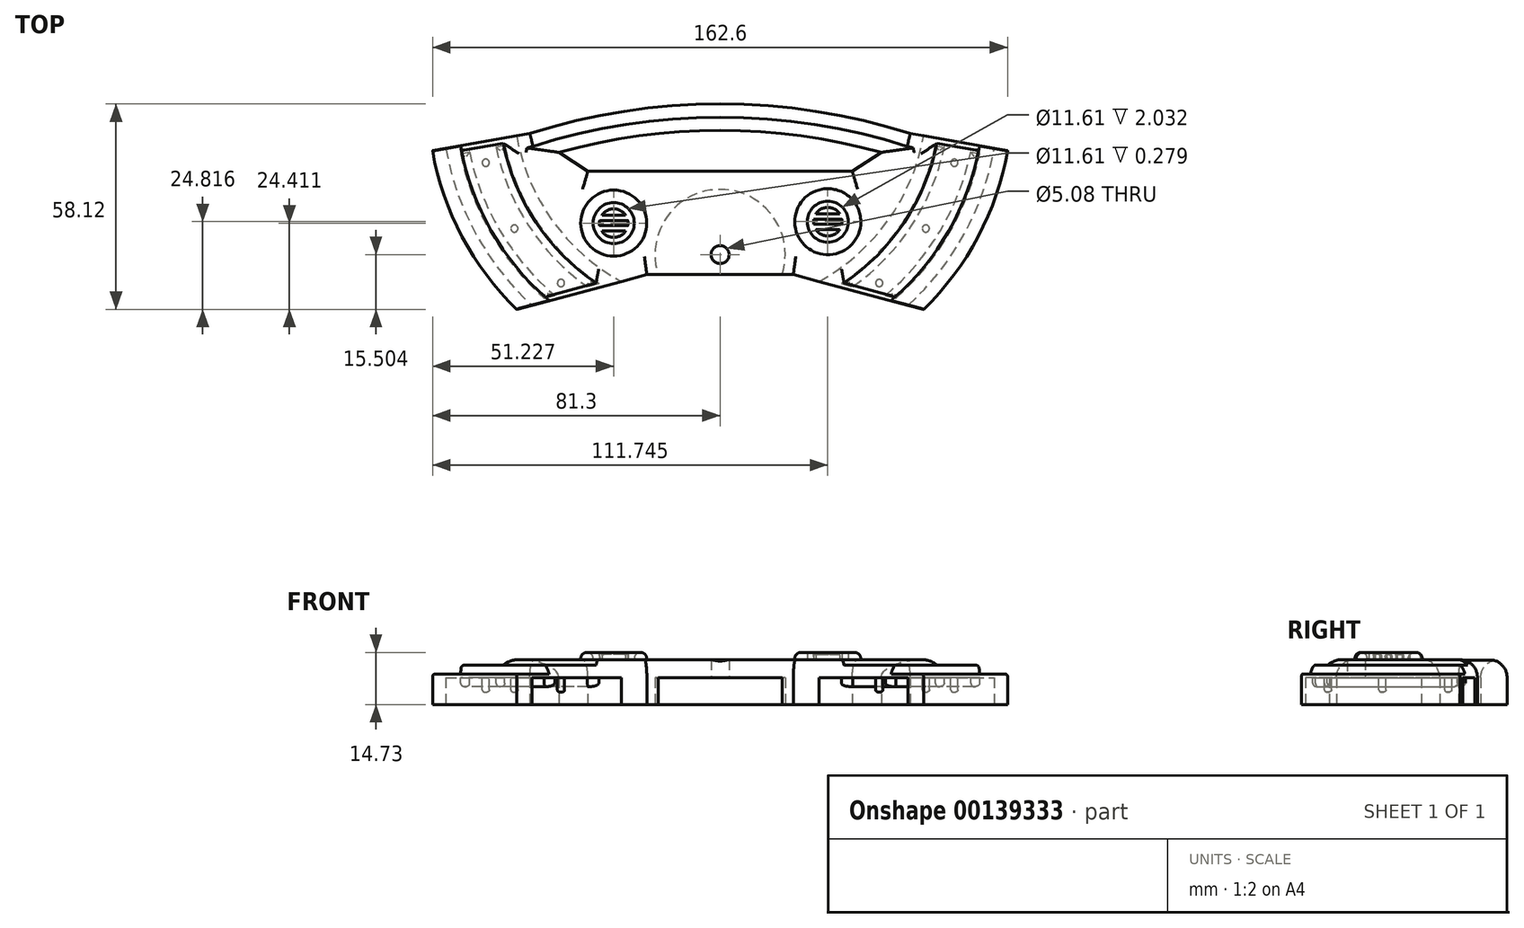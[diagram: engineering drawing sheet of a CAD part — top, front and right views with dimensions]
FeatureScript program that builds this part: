
annotation { "Feature Type Name" : "Feature", "Feature Type Description" : "" }
export const myFeature = defineFeature(function(context is Context, id is Id, definition is map)
    precondition{}
    {
        {
            var Q0;
            Q0=qCreatedBy(makeId("Top.planeOp"),FACE);
            var sketch = newSketch(context, id + "F0", { "sketchPlane" : qUnion([Q0])});
            skCircle(sketch, "E0", {"center": v(0, 0) * mm, "radius": 76.2 * mm, "construction": true});
            skCircle(sketch, "E1", {"center": v(0, 0) * mm, "radius": 60.96 * mm, "construction": true});
            skArc(sketch, "E2", {"start": v(-81.3, -14.33) * mm, "mid": v(-72.94, -38.65) * mm, "end": v(-57.5, -59.22) * mm});
            skLineSegment(sketch, "E3", {"start": v(0, 0) * mm, "end": v(-81.3, -14.33) * mm, "construction": true});
            skArc(sketch, "E4", {"start": v(81.3, -14.33) * mm, "mid": v(72.94, -38.65) * mm, "end": v(57.5, -59.22) * mm});
            skLineSegment(sketch, "E5", {"start": v(81.3, -14.33) * mm, "end": v(0, 0) * mm, "construction": true});
            skLineSegment(sketch, "E6", {"start": v(81.3, -14.33) * mm, "end": v(57.5, -59.22) * mm, "construction": true});
            skLineSegment(sketch, "E7", {"start": v(-81.3, -14.33) * mm, "end": v(-57.5, -59.22) * mm, "construction": true});
            skLineSegment(sketch, "E8", {"start": v(57.5, -59.22) * mm, "end": v(20.7, -49.36) * mm});
            skLineSegment(sketch, "E9", {"start": v(20.7, -49.36) * mm, "end": v(-20.7, -49.36) * mm});
            skLineSegment(sketch, "E10", {"start": v(-20.7, -49.36) * mm, "end": v(-57.5, -59.22) * mm});
            skLineSegment(sketch, "E11", {"start": v(-81.3, -14.33) * mm, "end": v(-53.78, -9.48) * mm});
            skLineSegment(sketch, "E12", {"start": v(-45.58, -14.8) * mm, "end": v(-37.38, -20.13) * mm});
            skLineSegment(sketch, "E13", {"start": v(-37.38, -20.13) * mm, "end": v(37.38, -20.13) * mm});
            skLineSegment(sketch, "E14", {"start": v(37.38, -20.13) * mm, "end": v(45.58, -14.8) * mm});
            skLineSegment(sketch, "E15", {"start": v(53.78, -9.48) * mm, "end": v(81.3, -14.33) * mm});
            skLineSegment(sketch, "E16", {"start": v(0, 0) * mm, "end": v(0, -177.8) * mm, "construction": true});
            skArc(sketch, "E17", {"start": v(-53.78, -9.48) * mm, "mid": v(0, -1.1) * mm, "end": v(53.78, -9.48) * mm});
            skArc(sketch, "E18", {"start": v(45.58, -14.8) * mm, "mid": v(0, -8.56) * mm, "end": v(-45.58, -14.8) * mm});
            skSolve(sketch);
        }
        {
            var Q0;
            Q0 = qSketchRegion(id + "F0", true);
            extrude(context, id + "F1", {"entities" : qUnion([Q0]), "depth" : 12.7 * mm});
        }
        {
            var Q0;
            Q0=qCreatedBy(makeId("Front.planeOp"),FACE);
            var sketch = newSketch(context, id + "F2", { "sketchPlane" : qUnion([Q0])});
            skLineSegment(sketch, "E19", {"start": v(62.5, 16.37) * mm, "end": v(62.5, 11.1) * mm});
            skLineSegment(sketch, "E20", {"start": v(62.5, 11.1) * mm, "end": v(74.5, 11.1) * mm});
            skLineSegment(sketch, "E21", {"start": v(74.5, 11.1) * mm, "end": v(74.5, 8.65) * mm});
            skLineSegment(sketch, "E22", {"start": v(74.5, 8.65) * mm, "end": v(83.99, 8.65) * mm});
            skLineSegment(sketch, "E23", {"start": v(83.99, 8.65) * mm, "end": v(83.99, 15.75) * mm});
            skLineSegment(sketch, "E24", {"start": v(83.99, 15.75) * mm, "end": v(62.5, 16.37) * mm});
            skSolve(sketch);
        }
        {
            var Q0;
            Q0=qCreatedBy(makeId("Front.planeOp"),FACE);
            var sketch = newSketch(context, id + "F3", { "sketchPlane" : qUnion([Q0])});
            skLineSegment(sketch, "E25", {"start": v(0, 99.5) * mm, "end": v(0, -112.08) * mm, "construction": true});
            skSolve(sketch);
        }
        {
            var Q0;
            Q0 = qSketchRegion(id + "F2", true);
            var Q1;
            Q1=sQuery(id+"F3.wireOp",EDGE,"E25");
            revolve(context, id + "F4", {"operationType" : NewBodyOperationType.REMOVE, "entities" : qUnion([Q0]), "axis" : qUnion([Q1]), "revolveType" : RevolveType.FULL, "oppositeDirection" : true});
        }
        {
            var Q0;
            Q0=makeQuery(id+"F1.opExtrude","CAP_FACE",FACE,{"disambiguationData":[OSD([sQuery(id+"F0.wireOp",EDGE,"E2"),sQuery(id+"F0.wireOp",EDGE,"E4"),sQuery(id+"F0.wireOp",EDGE,"E8"),sQuery(id+"F0.wireOp",EDGE,"E9"),sQuery(id+"F0.wireOp",EDGE,"E10"),sQuery(id+"F0.wireOp",EDGE,"E11"),sQuery(id+"F0.wireOp",EDGE,"E12"),sQuery(id+"F0.wireOp",EDGE,"E13"),sQuery(id+"F0.wireOp",EDGE,"E14"),sQuery(id+"F0.wireOp",EDGE,"E15"),sQuery(id+"F0.wireOp",EDGE,"E17"),sQuery(id+"F0.wireOp",EDGE,"E18")])],"isStart":false});
            fillet(context, id + "F5", {"entities" : qUnion([Q0]), "radius" : 5.08 * mm, "tangentPropagation" : true, "allowEdgeOverflow" : false});
        }
        {
            var Q0;
            Q0=makeQuery(id+"F1.opExtrude","CAP_FACE",FACE,{"disambiguationData":[OSD([sQuery(id+"F0.wireOp",EDGE,"E2"),sQuery(id+"F0.wireOp",EDGE,"E4"),sQuery(id+"F0.wireOp",EDGE,"E8"),sQuery(id+"F0.wireOp",EDGE,"E9"),sQuery(id+"F0.wireOp",EDGE,"E10"),sQuery(id+"F0.wireOp",EDGE,"E11"),sQuery(id+"F0.wireOp",EDGE,"E12"),sQuery(id+"F0.wireOp",EDGE,"E13"),sQuery(id+"F0.wireOp",EDGE,"E14"),sQuery(id+"F0.wireOp",EDGE,"E15"),sQuery(id+"F0.wireOp",EDGE,"E17"),sQuery(id+"F0.wireOp",EDGE,"E18")])],"isStart":false});
            var sketch = newSketch(context, id + "F6", { "sketchPlane" : qUnion([Q0])});
            skLineSegment(sketch, "E26", {"start": v(38.88, -25.21) * mm, "end": v(34.33, -47.75) * mm, "construction": true});
            skLineSegment(sketch, "E27", {"start": v(34.33, -47.75) * mm, "end": v(56.82, -15.18) * mm, "construction": true});
            skLineSegment(sketch, "E28", {"start": v(56.82, -15.18) * mm, "end": v(-56.82, -15.18) * mm, "construction": true});
            skLineSegment(sketch, "E29", {"start": v(-56.82, -15.18) * mm, "end": v(-34.33, -47.75) * mm, "construction": true});
            skLineSegment(sketch, "E30", {"start": v(-34.33, -47.75) * mm, "end": v(-38.88, -25.21) * mm, "construction": true});
            skLineSegment(sketch, "E31", {"start": v(-38.88, -25.21) * mm, "end": v(46.13, -36.48) * mm, "construction": true});
            skPoint(sketch, "E31.endSnap0", {"position": v(-36.6, -36.48) * mm});
            skLineSegment(sketch, "E32", {"start": v(46.13, -36.48) * mm, "end": v(-42.1, -36.48) * mm, "construction": true});
            skLineSegment(sketch, "E33", {"start": v(-42.1, -36.48) * mm, "end": v(38.88, -25.21) * mm, "construction": true});
            skLineSegment(sketch, "E34", {"start": v(21.38, -44.28) * mm, "end": v(38.88, -25.21) * mm, "construction": true});
            skLineSegment(sketch, "E35", {"start": v(-21.38, -44.28) * mm, "end": v(-38.88, -25.21) * mm, "construction": true});
            skCircle(sketch, "E36", {"center": v(30.44, -34.4) * mm, "radius": 9.33 * mm});
            skCircle(sketch, "E37", {"center": v(-30.07, -34.8) * mm, "radius": 9.33 * mm});
            skCircle(sketch, "E38", {"center": v(-30.07, -34.8) * mm, "radius": 5.8 * mm});
            skCircle(sketch, "E39", {"center": v(30.44, -34.4) * mm, "radius": 5.8 * mm});
            skSolve(sketch);
        }
        {
            var Q0;
            Q0 = qSketchRegion(id + "F6", true);
            extrude(context, id + "F7", {"entities" : qUnion([Q0]), "operationType" : NewBodyOperationType.ADD, "depth" : 2.03 * mm});
        }
        {
            var Q0;
            Q0=makeQuery(id+"F7.opExtrude","CAP_FACE",FACE,{"disambiguationData":[OSD([sQuery(id+"F6.wireOp",EDGE,"E37"),sQuery(id+"F6.wireOp",EDGE,"E38")])],"isStart":false});
            var Q1;
            Q1=makeQuery(id+"F7.opExtrude","CAP_EDGE",EDGE,{"disambiguationData":[OSD([sQuery(id+"F6.wireOp",EDGE,"E36")])],"isStart":false});
            fillet(context, id + "F8", {"entities" : qUnion([Q0, Q1]), "radius" : 1.75 * mm, "tangentPropagation" : true, "allowEdgeOverflow" : false});
        }
        {
            var Q0;
            Q0=makeQuery(id+"F7.boolean.opBoolean","SPLIT",FACE,{"disambiguationData":[TD([makeQuery(id+"F7.opExtrude","SWEPT_FACE",FACE,{"disambiguationData":[OSD([sQuery(id+"F6.wireOp",EDGE,"E38")])]})])],"derivedFrom":makeQuery(id+"F1.opExtrude","CAP_FACE",FACE,{"disambiguationData":[OSD([sQuery(id+"F0.wireOp",EDGE,"E2"),sQuery(id+"F0.wireOp",EDGE,"E4"),sQuery(id+"F0.wireOp",EDGE,"E8"),sQuery(id+"F0.wireOp",EDGE,"E9"),sQuery(id+"F0.wireOp",EDGE,"E10"),sQuery(id+"F0.wireOp",EDGE,"E11"),sQuery(id+"F0.wireOp",EDGE,"E12"),sQuery(id+"F0.wireOp",EDGE,"E13"),sQuery(id+"F0.wireOp",EDGE,"E14"),sQuery(id+"F0.wireOp",EDGE,"E15"),sQuery(id+"F0.wireOp",EDGE,"E17"),sQuery(id+"F0.wireOp",EDGE,"E18")])],"isStart":false})});
            var sketch = newSketch(context, id + "F9", { "sketchPlane" : qUnion([Q0])});
            skArc(sketch, "E40", {"start": v(-34.04, -34.07) * mm, "mid": v(-34.11, -34.8) * mm, "end": v(-34.04, -35.55) * mm});
            skLineSegment(sketch, "E41", {"start": v(-26.73, -32.55) * mm, "end": v(-33.42, -32.55) * mm});
            skLineSegment(sketch, "E42", {"start": v(-26.1, -34.07) * mm, "end": v(-34.04, -34.07) * mm});
            skLineSegment(sketch, "E43", {"start": v(-26.1, -35.55) * mm, "end": v(-34.04, -35.55) * mm});
            skLineSegment(sketch, "E44", {"start": v(-33.42, -37.07) * mm, "end": v(-26.73, -37.07) * mm});
            skArc(sketch, "E45.trimOffspring", {"start": v(-26.73, -32.55) * mm, "mid": v(-30.07, -30.77) * mm, "end": v(-33.42, -32.55) * mm});
            skArc(sketch, "E46.trimOffspring", {"start": v(-26.1, -35.55) * mm, "mid": v(-26.03, -34.8) * mm, "end": v(-26.1, -34.07) * mm});
            skArc(sketch, "E47.trimOffspring", {"start": v(-33.42, -37.07) * mm, "mid": v(-30.07, -38.85) * mm, "end": v(-26.73, -37.07) * mm});
            skSolve(sketch);
        }
        {
            var Q0;
            Q0=makeQuery(id+"F7.boolean.opBoolean","SPLIT",FACE,{"disambiguationData":[TD([makeQuery(id+"F7.opExtrude","SWEPT_FACE",FACE,{"disambiguationData":[OSD([sQuery(id+"F6.wireOp",EDGE,"E39")])]})])],"derivedFrom":makeQuery(id+"F1.opExtrude","CAP_FACE",FACE,{"disambiguationData":[OSD([sQuery(id+"F0.wireOp",EDGE,"E2"),sQuery(id+"F0.wireOp",EDGE,"E4"),sQuery(id+"F0.wireOp",EDGE,"E8"),sQuery(id+"F0.wireOp",EDGE,"E9"),sQuery(id+"F0.wireOp",EDGE,"E10"),sQuery(id+"F0.wireOp",EDGE,"E11"),sQuery(id+"F0.wireOp",EDGE,"E12"),sQuery(id+"F0.wireOp",EDGE,"E13"),sQuery(id+"F0.wireOp",EDGE,"E14"),sQuery(id+"F0.wireOp",EDGE,"E15"),sQuery(id+"F0.wireOp",EDGE,"E17"),sQuery(id+"F0.wireOp",EDGE,"E18")])],"isStart":false})});
            var sketch = newSketch(context, id + "F10", { "sketchPlane" : qUnion([Q0])});
            skArc(sketch, "E48", {"start": v(33.8, -32.14) * mm, "mid": v(30.44, -30.37) * mm, "end": v(27.1, -32.14) * mm});
            skLineSegment(sketch, "E49", {"start": v(27.1, -32.14) * mm, "end": v(33.8, -32.14) * mm});
            skLineSegment(sketch, "E50", {"start": v(34.42, -33.67) * mm, "end": v(26.47, -33.67) * mm});
            skLineSegment(sketch, "E51", {"start": v(26.47, -35.14) * mm, "end": v(34.42, -35.14) * mm});
            skLineSegment(sketch, "E52", {"start": v(33.8, -36.67) * mm, "end": v(27.1, -36.67) * mm});
            skArc(sketch, "E53.trimOffspring", {"start": v(26.47, -33.67) * mm, "mid": v(26.4, -34.4) * mm, "end": v(26.47, -35.14) * mm});
            skArc(sketch, "E54.trimOffspring", {"start": v(27.1, -36.67) * mm, "mid": v(30.44, -38.44) * mm, "end": v(33.8, -36.67) * mm});
            skArc(sketch, "E55.trimOffspring", {"start": v(34.42, -35.14) * mm, "mid": v(34.48, -34.4) * mm, "end": v(34.42, -33.67) * mm});
            skSolve(sketch);
        }
        {
            var Q0;
            Q0 = qSketchRegion(id + "F9", true);
            extrude(context, id + "F11", {"entities" : qUnion([Q0]), "operationType" : NewBodyOperationType.ADD, "depth" : 1.52 * mm});
        }
        {
            var Q0;
            Q0=makeQuery(id+"F11.opExtrude","CAP_EDGE",EDGE,{"disambiguationData":[OSD([sQuery(id+"F9.wireOp",EDGE,"E42")])],"isStart":false});
            var Q1;
            Q1=makeQuery(id+"F11.opExtrude","CAP_EDGE",EDGE,{"disambiguationData":[OSD([sQuery(id+"F9.wireOp",EDGE,"E43")])],"isStart":false});
            fillet(context, id + "F12", {"entities" : qUnion([Q0, Q1]), "radius" : 0.7 * mm, "tangentPropagation" : true, "allowEdgeOverflow" : false});
        }
        {
            var Q0;
            Q0=makeQuery(id+"F11.opExtrude","CAP_FACE",FACE,{"disambiguationData":[OSD([sQuery(id+"F9.wireOp",EDGE,"E41"),sQuery(id+"F9.wireOp",EDGE,"E45.trimOffspring")])],"isStart":false});
            var Q1;
            Q1=makeQuery(id+"F11.opExtrude","CAP_FACE",FACE,{"disambiguationData":[OSD([sQuery(id+"F9.wireOp",EDGE,"E44"),sQuery(id+"F9.wireOp",EDGE,"E47.trimOffspring")])],"isStart":false});
            fillet(context, id + "F13", {"entities" : qUnion([Q0, Q1]), "radius" : 0.25 * mm, "tangentPropagation" : true, "allowEdgeOverflow" : false});
        }
        {
            var Q0;
            Q0 = qSketchRegion(id + "F10", true);
            extrude(context, id + "F14", {"entities" : qUnion([Q0]), "operationType" : NewBodyOperationType.ADD, "depth" : 1.52 * mm});
        }
        {
            var Q0;
            Q0=makeQuery(id+"F4.boolean.opBoolean","COPY",EDGE,{"disambiguationData":[OD(1.0)],"derivedFrom":makeQuery(id+"F4.opRevolve","SWEPT_EDGE",EDGE,{"disambiguationData":[OSD([sQuery(id+"F2.wireOp",EDGE,"E20"),sQuery(id+"F2.wireOp",EDGE,"E21")])]})});
            var Q1;
            Q1=makeQuery(id+"F4.boolean.opBoolean","INTERSECT",EDGE,{"derivedFrom":[makeQuery(id+"F1.opExtrude","SWEPT_FACE",FACE,{"disambiguationData":[OSD([sQuery(id+"F0.wireOp",EDGE,"E2")])]}),makeQuery(id+"F4.opRevolve","SWEPT_FACE",FACE,{"disambiguationData":[OSD([sQuery(id+"F2.wireOp",EDGE,"E22")])]})]});
            var Q2;
            Q2=makeQuery(id+"F4.boolean.opBoolean","COPY",EDGE,{"disambiguationData":[OD(0.0)],"derivedFrom":makeQuery(id+"F4.opRevolve","SWEPT_EDGE",EDGE,{"disambiguationData":[OSD([sQuery(id+"F2.wireOp",EDGE,"E20"),sQuery(id+"F2.wireOp",EDGE,"E21")])]})});
            var Q3;
            Q3=makeQuery(id+"F4.boolean.opBoolean","INTERSECT",EDGE,{"derivedFrom":[makeQuery(id+"F1.opExtrude","SWEPT_FACE",FACE,{"disambiguationData":[OSD([sQuery(id+"F0.wireOp",EDGE,"E4")])]}),makeQuery(id+"F4.opRevolve","SWEPT_FACE",FACE,{"disambiguationData":[OSD([sQuery(id+"F2.wireOp",EDGE,"E22")])]})]});
            fillet(context, id + "F15", {"entities" : qUnion([Q0, Q1, Q2, Q3]), "radius" : 0.76 * mm, "tangentPropagation" : true, "allowEdgeOverflow" : false});
        }
        {
            var Q0;
            Q0=qCreatedBy(makeId("Top.planeOp"),FACE);
            var sketch = newSketch(context, id + "F16", { "sketchPlane" : qUnion([Q0])});
            skCircle(sketch, "E56", {"center": v(0, 0) * mm, "radius": 78.74 * mm});
            skCircle(sketch, "E57", {"center": v(0, 0) * mm, "radius": 58.42 * mm});
            skSolve(sketch);
        }
        {
            var Q0;
            Q0 = qSketchRegion(id + "F16", true);
            extrude(context, id + "F17", {"entities" : qUnion([Q0]), "operationType" : NewBodyOperationType.REMOVE, "depth" : 7.62 * mm});
        }
        {
            var Q0;
            Q0=makeQuery(id+"F14.opExtrude","CAP_EDGE",EDGE,{"disambiguationData":[OSD([sQuery(id+"F10.wireOp",EDGE,"E50")])],"isStart":false});
            var Q1;
            Q1=makeQuery(id+"F14.opExtrude","CAP_EDGE",EDGE,{"disambiguationData":[OSD([sQuery(id+"F10.wireOp",EDGE,"E51")])],"isStart":false});
            fillet(context, id + "F18", {"entities" : qUnion([Q0, Q1]), "radius" : 0.71 * mm, "tangentPropagation" : true, "allowEdgeOverflow" : false});
        }
        {
            var Q0;
            Q0=makeQuery(id+"F14.opExtrude","CAP_FACE",FACE,{"disambiguationData":[OSD([sQuery(id+"F10.wireOp",EDGE,"E48"),sQuery(id+"F10.wireOp",EDGE,"E49")])],"isStart":false});
            var Q1;
            Q1=makeQuery(id+"F14.opExtrude","CAP_FACE",FACE,{"disambiguationData":[OSD([sQuery(id+"F10.wireOp",EDGE,"E52"),sQuery(id+"F10.wireOp",EDGE,"E54.trimOffspring")])],"isStart":false});
            fillet(context, id + "F19", {"entities" : qUnion([Q0, Q1]), "radius" : 0.25 * mm, "tangentPropagation" : true, "allowEdgeOverflow" : false});
        }
        {
            var Q0;
            Q0=makeQuery(id+"F17.boolean.opBoolean","COPY",FACE,{"disambiguationData":[OD(1.0)],"derivedFrom":makeQuery(id+"F17.opExtrude","CAP_FACE",FACE,{"disambiguationData":[OSD([sQuery(id+"F16.wireOp",EDGE,"E56"),sQuery(id+"F16.wireOp",EDGE,"E57")])],"isStart":false})});
            var sketch = newSketch(context, id + "F20", { "sketchPlane" : qUnion([Q0])});
            skCircle(sketch, "E58", {"center": v(0, 0) * mm, "radius": 76.2 * mm, "construction": true});
            skCircle(sketch, "E59", {"center": v(0, 0) * mm, "radius": 60.96 * mm, "construction": true});
            skLineSegment(sketch, "E60", {"start": v(0, 0) * mm, "end": v(66.24, 17.75) * mm, "construction": true});
            skCircle(sketch, "E61", {"center": v(0, 0) * mm, "radius": 68.58 * mm, "construction": true});
            skLineSegment(sketch, "E62", {"start": v(0, 0) * mm, "end": v(58.16, 36.34) * mm, "construction": true});
            skLineSegment(sketch, "E63", {"start": v(0, 0) * mm, "end": v(45, 51.76) * mm, "construction": true});
            skCircle(sketch, "E64", {"center": v(66.24, 17.75) * mm, "radius": 1.02 * mm});
            skCircle(sketch, "E65", {"center": v(58.16, 36.34) * mm, "radius": 1.02 * mm});
            skCircle(sketch, "E66", {"center": v(45, 51.76) * mm, "radius": 1.02 * mm});
            skCircle(sketch, "E67.MirrorC", {"center": v(-66.24, 17.75) * mm, "radius": 1.02 * mm});
            skCircle(sketch, "E68.MirrorC", {"center": v(-58.16, 36.34) * mm, "radius": 1.02 * mm});
            skCircle(sketch, "E69.MirrorC", {"center": v(-45, 51.76) * mm, "radius": 1.02 * mm});
            skSolve(sketch);
        }
        {
            var Q0;
            Q0 = qSketchRegion(id + "F20", true);
            extrude(context, id + "F21", {"entities" : qUnion([Q0]), "operationType" : NewBodyOperationType.ADD, "depth" : 4.06 * mm});
        }
        {
            var Q0;
            Q0=makeQuery(id+"F21.opExtrude","CAP_EDGE",EDGE,{"disambiguationData":[OSD([sQuery(id+"F20.wireOp",EDGE,"E69.MirrorC")])],"isStart":false});
            var Q1;
            Q1=makeQuery(id+"F21.opExtrude","CAP_EDGE",EDGE,{"disambiguationData":[OSD([sQuery(id+"F20.wireOp",EDGE,"E68.MirrorC")])],"isStart":false});
            var Q2;
            Q2=makeQuery(id+"F21.opExtrude","CAP_FACE",FACE,{"disambiguationData":[OSD([sQuery(id+"F20.wireOp",EDGE,"E67.MirrorC")])],"isStart":false});
            var Q3;
            Q3=makeQuery(id+"F21.opExtrude","CAP_FACE",FACE,{"disambiguationData":[OSD([sQuery(id+"F20.wireOp",EDGE,"E66")])],"isStart":false});
            var Q4;
            Q4=makeQuery(id+"F21.opExtrude","CAP_EDGE",EDGE,{"disambiguationData":[OSD([sQuery(id+"F20.wireOp",EDGE,"E65")])],"isStart":false});
            var Q5;
            Q5=makeQuery(id+"F21.opExtrude","CAP_EDGE",EDGE,{"disambiguationData":[OSD([sQuery(id+"F20.wireOp",EDGE,"E64")])],"isStart":false});
            fillet(context, id + "F22", {"entities" : qUnion([Q0, Q1, Q2, Q3, Q4, Q5]), "radius" : 0.64 * mm, "tangentPropagation" : true, "allowEdgeOverflow" : false});
        }
        {
            var Q0;
            Q0=makeQuery(id+"F17.boolean.opBoolean","COPY",FACE,{"disambiguationData":[OD(1.0)],"derivedFrom":makeQuery(id+"F17.opExtrude","CAP_FACE",FACE,{"disambiguationData":[OSD([sQuery(id+"F16.wireOp",EDGE,"E56"),sQuery(id+"F16.wireOp",EDGE,"E57")])],"isStart":false})});
            var sketch = newSketch(context, id + "F23", { "sketchPlane" : qUnion([Q0])});
            skArc(sketch, "E70", {"start": v(-37.52, 52.8) * mm, "mid": v(-54.16, 35.52) * mm, "end": v(-63.37, 13.37) * mm});
            skArc(sketch, "E71", {"start": v(-46.75, 55.27) * mm, "mid": v(-62.21, 37.01) * mm, "end": v(-70.88, 14.7) * mm});
            skArc(sketch, "E72", {"start": v(-49.71, 56.07) * mm, "mid": v(-64.86, 37.52) * mm, "end": v(-73.38, 15.15) * mm});
            skLineSegment(sketch, "E73", {"start": v(-53.19, 58.06) * mm, "end": v(-14.7, 47.75) * mm, "construction": true});
            skLineSegment(sketch, "E74.MirrorCS", {"start": v(53.19, 58.06) * mm, "end": v(14.7, 47.75) * mm, "construction": true});
            skLineSegment(sketch, "E75", {"start": v(-77.54, 13.67) * mm, "end": v(-57.53, 10.14) * mm, "construction": true});
            skLineSegment(sketch, "E76.MirrorCS", {"start": v(77.54, 13.67) * mm, "end": v(57.53, 10.14) * mm, "construction": true});
            skArc(sketch, "E77.trimOffspring", {"start": v(63.37, 13.37) * mm, "mid": v(54.16, 35.52) * mm, "end": v(37.52, 52.8) * mm});
            skArc(sketch, "E78.trimOffspring", {"start": v(73.38, 15.15) * mm, "mid": v(64.86, 37.52) * mm, "end": v(49.71, 56.07) * mm});
            skArc(sketch, "E79.trimOffspring", {"start": v(70.88, 14.7) * mm, "mid": v(62.21, 37.01) * mm, "end": v(46.75, 55.27) * mm});
            skLineSegment(sketch, "E80", {"start": v(-54.08, 57.23) * mm, "end": v(-15.24, 46.83) * mm, "construction": true});
            skLineSegment(sketch, "E81", {"start": v(-77.13, 15.82) * mm, "end": v(-46.34, 10.34) * mm, "construction": true});
            skLineSegment(sketch, "E82.MirrorCS", {"start": v(54.08, 57.23) * mm, "end": v(37.52, 52.8) * mm, "construction": true});
            skLineSegment(sketch, "E83.MirrorCS", {"start": v(77.13, 15.82) * mm, "end": v(65.88, 13.82) * mm, "construction": true});
            skLineSegment(sketch, "E84", {"start": v(-49.71, 56.07) * mm, "end": v(-46.75, 55.27) * mm});
            skLineSegment(sketch, "E85", {"start": v(-40.66, 53.64) * mm, "end": v(-37.52, 52.8) * mm});
            skLineSegment(sketch, "E86", {"start": v(-73.38, 15.15) * mm, "end": v(-70.88, 14.7) * mm});
            skLineSegment(sketch, "E87", {"start": v(-65.88, 13.82) * mm, "end": v(-63.37, 13.37) * mm});
            skLineSegment(sketch, "E88", {"start": v(63.37, 13.37) * mm, "end": v(65.88, 13.82) * mm});
            skLineSegment(sketch, "E89", {"start": v(70.88, 14.7) * mm, "end": v(73.38, 15.15) * mm});
            skLineSegment(sketch, "E90", {"start": v(37.52, 52.8) * mm, "end": v(40.66, 53.64) * mm});
            skLineSegment(sketch, "E91", {"start": v(46.75, 55.27) * mm, "end": v(49.71, 56.07) * mm});
            skArc(sketch, "E92", {"start": v(60.87, 12.93) * mm, "mid": v(51.42, 35.05) * mm, "end": v(34.29, 51.93) * mm});
            skArc(sketch, "E93", {"start": v(-36.4, 53.57) * mm, "mid": v(0, -64.77) * mm, "end": v(36.4, 53.57) * mm, "construction": true});
            skLineSegment(sketch, "E94.trimOffspring", {"start": v(63.37, 13.37) * mm, "end": v(46.34, 10.34) * mm, "construction": true});
            skLineSegment(sketch, "E95.trimOffspring", {"start": v(34.29, 51.93) * mm, "end": v(15.24, 46.83) * mm, "construction": true});
            skArc(sketch, "E96.trimOffspring", {"start": v(-34.29, 51.93) * mm, "mid": v(-51.42, 35.05) * mm, "end": v(-60.87, 12.93) * mm});
            skLineSegment(sketch, "E97", {"start": v(-34.29, 51.93) * mm, "end": v(-37.52, 52.8) * mm});
            skLineSegment(sketch, "E98", {"start": v(-60.87, 12.93) * mm, "end": v(-63.37, 13.37) * mm});
            skLineSegment(sketch, "E99", {"start": v(60.87, 12.93) * mm, "end": v(63.37, 13.37) * mm});
            skLineSegment(sketch, "E100", {"start": v(34.29, 51.93) * mm, "end": v(37.52, 52.8) * mm});
            skSolve(sketch);
        }
        {
            var Q0;
            Q0 = qSketchRegion(id + "F23", true);
            extrude(context, id + "F24", {"entities" : qUnion([Q0]), "operationType" : NewBodyOperationType.ADD, "depth" : 2.54 * mm});
        }
        {
            var Q0;
            Q0=makeQuery(id+"F24.opExtrude","CAP_FACE",FACE,{"disambiguationData":[OSD([sQuery(id+"F23.wireOp",EDGE,"e2b732bb-df48-4231-8cf6-9f20eeaedfbb.trimOffspring"),sQuery(id+"F23.wireOp",EDGE,"E77.trimOffspring"),sQuery(id+"F23.wireOp",EDGE,"E88"),sQuery(id+"F23.wireOp",EDGE,"E90")])],"isStart":false});
            var Q1;
            Q1=makeQuery(id+"F24.opExtrude","CAP_FACE",FACE,{"disambiguationData":[OSD([sQuery(id+"F23.wireOp",EDGE,"E78.trimOffspring"),sQuery(id+"F23.wireOp",EDGE,"E79.trimOffspring"),sQuery(id+"F23.wireOp",EDGE,"E89"),sQuery(id+"F23.wireOp",EDGE,"E91")])],"isStart":false});
            var Q2;
            Q2=makeQuery(id+"F24.opExtrude","CAP_FACE",FACE,{"disambiguationData":[OSD([sQuery(id+"F23.wireOp",EDGE,"E71"),sQuery(id+"F23.wireOp",EDGE,"E72"),sQuery(id+"F23.wireOp",EDGE,"E84"),sQuery(id+"F23.wireOp",EDGE,"E86")])],"isStart":false});
            var Q3;
            Q3=makeQuery(id+"F24.opExtrude","CAP_FACE",FACE,{"disambiguationData":[OSD([sQuery(id+"F23.wireOp",EDGE,"HvzRBNUH-Ws5O-fryz-vqn3-pfWEQRTrrrLi"),sQuery(id+"F23.wireOp",EDGE,"E70"),sQuery(id+"F23.wireOp",EDGE,"E85"),sQuery(id+"F23.wireOp",EDGE,"E87")])],"isStart":false});
            fillet(context, id + "F25", {"entities" : qUnion([Q0, Q1, Q2, Q3]), "radius" : 1.02 * mm, "tangentPropagation" : true, "allowEdgeOverflow" : false});
        }
        {
            var Q0;
            {var subQ0=sQuery(id+"F0.wireOp",EDGE,"E18");var subQ1=sQuery(id+"F0.wireOp",EDGE,"E15");var subQ2=sQuery(id+"F0.wireOp",EDGE,"E14");var subQ3=sQuery(id+"F0.wireOp",EDGE,"E13");var subQ4=sQuery(id+"F0.wireOp",EDGE,"E12");var subQ5=sQuery(id+"F0.wireOp",EDGE,"E8");var subQ6=sQuery(id+"F0.wireOp",EDGE,"E17");var subQ7=sQuery(id+"F0.wireOp",EDGE,"E9");var subQ8=sQuery(id+"F0.wireOp",EDGE,"E10");var subQ9=sQuery(id+"F0.wireOp",EDGE,"E11");Q0=makeQuery(id+"F17.boolean.opBoolean","SPLIT",FACE,{"disambiguationData":[TD([makeQuery(id+"F1.opExtrude","SWEPT_FACE",FACE,{"disambiguationData":[OSD([subQ7])]})])],"derivedFrom":makeQuery(id+"F1.opExtrude","CAP_FACE",FACE,{"disambiguationData":[OSD([sQuery(id+"F0.wireOp",EDGE,"E2"),sQuery(id+"F0.wireOp",EDGE,"E4"),subQ5,subQ7,subQ8,subQ9,subQ4,subQ3,subQ2,subQ1,subQ6,subQ0])],"isStart":true})});}
            var sketch = newSketch(context, id + "F26", { "sketchPlane" : qUnion([Q0])});
            skCircle(sketch, "E101", {"center": v(0, 0) * mm, "radius": 60.96 * mm, "construction": true});
            skCircle(sketch, "E102", {"center": v(0, 0) * mm, "radius": 76.2 * mm, "construction": true});
            skCircle(sketch, "E103", {"center": v(0, 0) * mm, "radius": 58.42 * mm, "construction": true});
            skLineSegment(sketch, "E104", {"start": v(0, 0) * mm, "end": v(0, 98.07) * mm, "construction": true});
            skCircle(sketch, "E105", {"center": v(0, 43.7) * mm, "radius": 18.41 * mm});
            skCircle(sketch, "E106", {"center": v(0, 0) * mm, "radius": 59.7 * mm, "construction": true});
            skSolve(sketch);
        }
        {
            var Q0;
            Q0 = qSketchRegion(id + "F26", true);
            extrude(context, id + "F27", {"entities" : qUnion([Q0]), "operationType" : NewBodyOperationType.REMOVE, "oppositeDirection" : true, "depth" : 7.62 * mm});
        }
        {
            var Q0;
            {var subQ0=sQuery(id+"F26.wireOp",EDGE,"E105");var subQ1=makeQuery(id+"F1.opExtrude","CAP_EDGE",EDGE,{"disambiguationData":[OSD([sQuery(id+"F0.wireOp",EDGE,"E9")])],"isStart":true});var subQ2=makeQuery(id+"F26.imprint","INTERSECT",VERTEX,{"disambiguationData":[OD(0.0)],"derivedFrom":[subQ1,subQ0]});Q0=makeQuery(id+"F26.imprint","IMPRINT",FACE,{"disambiguationData":[TD([[makeQuery(id+"F26.imprint","IMPRINT",EDGE,{"disambiguationData":[TD([[subQ2,1.0]])],"derivedFrom":subQ0}),1.0]])]});}
            var sketch = newSketch(context, id + "F28", { "sketchPlane" : qUnion([Q0])});
            skCircle(sketch, "E107", {"center": v(0, 43.72) * mm, "radius": 2.54 * mm});
            skSolve(sketch);
        }
        {
            var Q0;
            Q0 = qSketchRegion(id + "F28", true);
            extrude(context, id + "F29", {"entities" : qUnion([Q0]), "operationType" : NewBodyOperationType.REMOVE, "oppositeDirection" : true, "depth" : 25.4 * mm});
        }
    });
